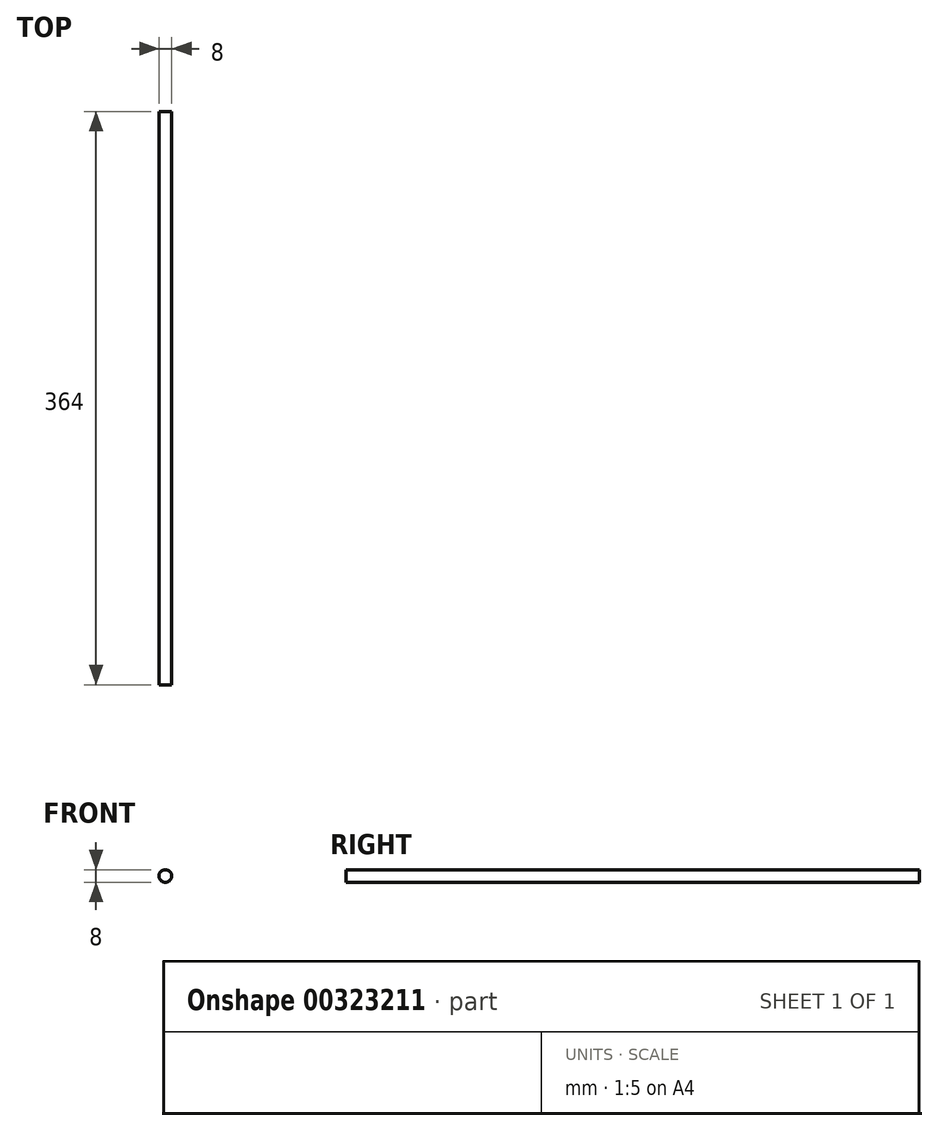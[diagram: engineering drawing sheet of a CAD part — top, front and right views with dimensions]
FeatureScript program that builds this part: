
annotation { "Feature Type Name" : "Feature", "Feature Type Description" : "" }
export const myFeature = defineFeature(function(context is Context, id is Id, definition is map)
    precondition{}
    {
        {
            var Q0;
            Q0=qCreatedBy(makeId("Front.planeOp"),FACE);
            var sketch = newSketch(context, id + "F0", { "sketchPlane" : qUnion([Q0])});
            skCircle(sketch, "E0", {"center": v(0, 0) * mm, "radius": 4 * mm});
            skSolve(sketch);
        }
        {
            var Q0;
            Q0=qSketchRegion(id+"F0",true);
            extrude(context, id + "F1", {"entities" : qUnion([Q0]), "endBound" : BoundingType.SYMMETRIC, "depth" : 364 * mm});
        }
    });
